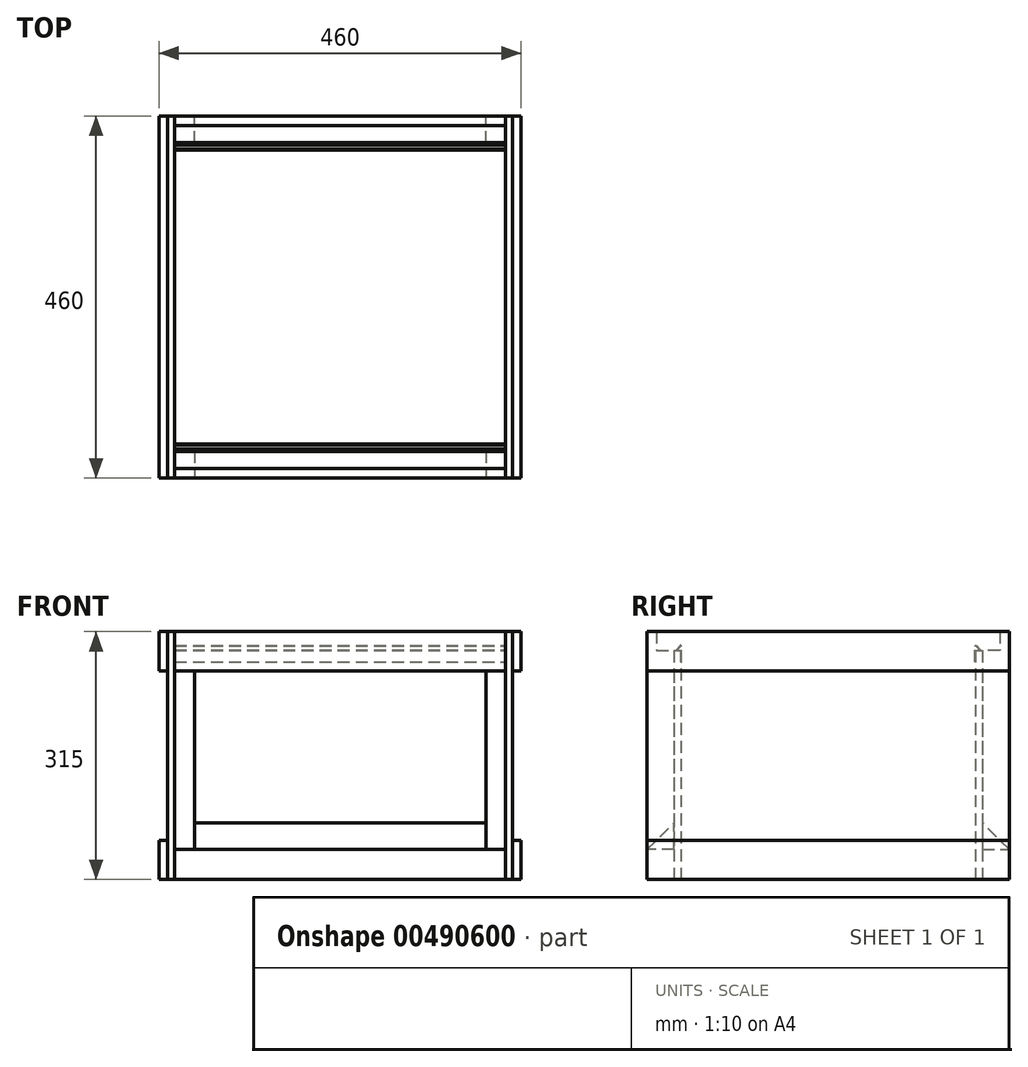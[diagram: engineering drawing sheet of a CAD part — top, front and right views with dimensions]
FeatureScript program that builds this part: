
annotation { "Feature Type Name" : "Feature", "Feature Type Description" : "" }
export const myFeature = defineFeature(function(context is Context, id is Id, definition is map)
    precondition{}
    {
        {
            var Q0;
            Q0=qCreatedBy(makeId("Right.planeOp"),FACE);
            var sketch = newSketch(context, id + "F0", { "sketchPlane" : qUnion([Q0])});
            skLineSegment(sketch, "E0", {"start": v(231.18, 0) * mm, "end": v(231.18, 279.77) * mm, "construction": true});
            skLineSegment(sketch, "E1.right", {"start": v(44.18, 288.91) * mm, "end": v(44.18, -2.09) * mm});
            skLineSegment(sketch, "E2.MirrorCS", {"start": v(418.18, 288.91) * mm, "end": v(418.18, -2.09) * mm});
            skLineSegment(sketch, "E3", {"start": v(35.18, 288.91) * mm, "end": v(35.18, -2.09) * mm});
            skLineSegment(sketch, "E4", {"start": v(427.18, 288.91) * mm, "end": v(427.18, -2.09) * mm});
            skPoint(sketch, "E5.orphan", {"position": v(26.18, 290.5) * mm});
            skPoint(sketch, "E6.MirrorCS.start.orphan", {"position": v(436.18, 290.5) * mm});
            skPoint(sketch, "E1.bottom.end.orphan", {"position": v(44.18, 290.5) * mm});
            skPoint(sketch, "E1.bottom.start.orphan", {"position": v(35.18, 290.5) * mm});
            skPoint(sketch, "E7.MirrorCS.end.orphan", {"position": v(418.18, 290.5) * mm});
            skPoint(sketch, "E7.MirrorCS.start.orphan", {"position": v(427.18, 290.5) * mm});
            skLineSegment(sketch, "E8", {"start": v(35.18, 288.91) * mm, "end": v(44.18, 288.91) * mm});
            skLineSegment(sketch, "E9.trimOffspring", {"start": v(418.18, 288.91) * mm, "end": v(427.18, 288.91) * mm});
            skLineSegment(sketch, "E10.0", {"start": v(35.18, -2.09) * mm, "end": v(44.18, -2.09) * mm});
            skLineSegment(sketch, "E11.0", {"start": v(427.18, -2.09) * mm, "end": v(418.18, -2.09) * mm});
            skPoint(sketch, "E12.MirrorCS.start.orphan", {"position": v(421.18, 288.91) * mm});
            skPoint(sketch, "E13.MirrorCS.end.orphan", {"position": v(418.18, 270.91) * mm});
            skPoint(sketch, "E13.MirrorCS.start.orphan", {"position": v(421.18, 270.91) * mm});
            skPoint(sketch, "E14.start.orphan", {"position": v(41.18, 288.91) * mm});
            skPoint(sketch, "E15.end.orphan", {"position": v(44.18, 270.91) * mm});
            skPoint(sketch, "E15.start.orphan", {"position": v(41.18, 270.91) * mm});
            skSolve(sketch);
        }
        {
            var Q0;
            Q0=qSketchRegion(id+"F0",true);
            extrude(context, id + "F1", {"entities" : qUnion([Q0]), "depth" : 420 * mm, "symmetric" : true});
        }
        {
            var Q0;
            Q0=qCreatedBy(makeId("Right.planeOp"),FACE);
            var sketch = newSketch(context, id + "F2", { "sketchPlane" : qUnion([Q0])});
            skLineSegment(sketch, "E16", {"start": v(1.18, -2.09) * mm, "end": v(1.18, 35.91) * mm});
            skLineSegment(sketch, "E17", {"start": v(231.18, 0) * mm, "end": v(231.18, 279.77) * mm, "construction": true});
            skLineSegment(sketch, "E18", {"start": v(1.18, 312.91) * mm, "end": v(13.18, 312.91) * mm});
            skLineSegment(sketch, "E19", {"start": v(13.18, 312.91) * mm, "end": v(13.18, 288.91) * mm});
            skLineSegment(sketch, "E20", {"start": v(35.18, 262.91) * mm, "end": v(1.18, 262.91) * mm});
            skLineSegment(sketch, "E21", {"start": v(1.18, -2.09) * mm, "end": v(35.18, -2.09) * mm});
            skLineSegment(sketch, "E22", {"start": v(35.18, 35.91) * mm, "end": v(1.18, 35.91) * mm});
            skLineSegment(sketch, "E23.trimOffspring", {"start": v(1.18, 262.91) * mm, "end": v(1.18, 312.91) * mm});
            skLineSegment(sketch, "E24.0", {"start": v(13.18, 288.91) * mm, "end": v(35.18, 288.91) * mm});
            skPoint(sketch, "E25.orphan", {"position": v(35.18, 288.91) * mm});
            skLineSegment(sketch, "E26.0", {"start": v(35.18, 288.91) * mm, "end": v(35.18, 262.91) * mm});
            skPoint(sketch, "E27.orphan", {"position": v(39.86, 35.91) * mm});
            skLineSegment(sketch, "E28.trimOffspring", {"start": v(35.18, 35.91) * mm, "end": v(35.18, -2.09) * mm});
            skPoint(sketch, "E29.orphan", {"position": v(35.18, -2.09) * mm});
            skLineSegment(sketch, "E30.MirrorCS", {"start": v(461.18, 312.91) * mm, "end": v(449.18, 312.91) * mm});
            skLineSegment(sketch, "E31.MirrorCS", {"start": v(449.18, 288.91) * mm, "end": v(427.18, 288.91) * mm});
            skLineSegment(sketch, "E32.MirrorCS", {"start": v(427.18, 288.91) * mm, "end": v(427.18, 262.91) * mm});
            skLineSegment(sketch, "E33.MirrorCS", {"start": v(461.18, -2.09) * mm, "end": v(461.18, 35.91) * mm});
            skPoint(sketch, "E34.MirrorP", {"position": v(427.18, 288.91) * mm});
            skLineSegment(sketch, "E35.MirrorCS", {"start": v(427.18, 262.91) * mm, "end": v(461.18, 262.91) * mm});
            skPoint(sketch, "E36.MirrorP", {"position": v(422.5, 35.91) * mm});
            skLineSegment(sketch, "E37.MirrorCS", {"start": v(461.18, 262.91) * mm, "end": v(461.18, 312.91) * mm});
            skLineSegment(sketch, "E38.MirrorCS", {"start": v(449.18, 312.91) * mm, "end": v(449.18, 288.91) * mm});
            skPoint(sketch, "E39.MirrorP", {"position": v(427.18, -2.09) * mm});
            skLineSegment(sketch, "E40.MirrorCS", {"start": v(427.18, 35.91) * mm, "end": v(461.18, 35.91) * mm});
            skLineSegment(sketch, "E41.MirrorCS", {"start": v(427.18, 35.91) * mm, "end": v(427.18, -2.09) * mm});
            skLineSegment(sketch, "E42.MirrorCS", {"start": v(461.18, -2.09) * mm, "end": v(427.18, -2.09) * mm});
            skSolve(sketch);
        }
        {
            var Q0;
            Q0=qSketchRegion(id+"F2",true);
            extrude(context, id + "F3", {"entities" : qUnion([Q0]), "depth" : 420 * mm, "symmetric" : true});
        }
        {
            var Q0;
            Q0=makeQuery(id+"F1.opExtrude","CAP_FACE",FACE,{"disambiguationData":[OSD([sQuery(id+"F0.wireOp",EDGE,"E1.right"),sQuery(id+"F0.wireOp",EDGE,"E3"),sQuery(id+"F0.wireOp",EDGE,"QR00Nk12-EYIH-hDG3-dkOs-eiUDFboGELUt"),sQuery(id+"F0.wireOp",EDGE,"E8"),sQuery(id+"F0.wireOp",EDGE,"E14"),sQuery(id+"F0.wireOp",EDGE,"E15")])],"isStart":false});
            var sketch = newSketch(context, id + "F4", { "sketchPlane" : qUnion([Q0])});
            skLineSegment(sketch, "E43.1", {"start": v(44.18, 293.91) * mm, "end": v(44.18, 274.51) * mm});
            skLineSegment(sketch, "E44", {"start": v(38.68, 288.91) * mm, "end": v(43.12, 294.3) * mm});
            skArc(sketch, "E45.filletArc", {"start": v(44.18, 293.91) * mm, "mid": v(43.78, 294.48) * mm, "end": v(43.12, 294.3) * mm});
            skLineSegment(sketch, "E46.0", {"start": v(44.73, 293.91) * mm, "end": v(44.73, 274.51) * mm});
            skArc(sketch, "E46.1", {"start": v(44.73, 293.91) * mm, "mid": v(44.52, 294.57) * mm, "end": v(43.97, 295) * mm});
            skLineSegment(sketch, "E46.2", {"start": v(38.25, 289.26) * mm, "end": v(42.7, 294.64) * mm});
            skLineSegment(sketch, "E47", {"start": v(44.73, 274.51) * mm, "end": v(44.18, 274.51) * mm});
            skLineSegment(sketch, "E48", {"start": v(38.25, 289.26) * mm, "end": v(38.68, 288.91) * mm});
            skLineSegment(sketch, "E49", {"start": v(43.2, 295) * mm, "end": v(43.97, 295) * mm});
            skPoint(sketch, "E49.startSnap0", {"position": v(43.97, 295) * mm});
            skArc(sketch, "E50.trimOffspring", {"start": v(43.2, 295) * mm, "mid": v(42.92, 294.85) * mm, "end": v(42.7, 294.64) * mm});
            skPoint(sketch, "E51.orphan", {"position": v(42.8, 295) * mm});
            skSolve(sketch);
        }
        {
            var Q0;
            Q0 = qSketchRegion(id + "F4", true);
            var Q1;
            Q1=makeQuery(id+"F1.opExtrude","CAP_FACE",FACE,{"disambiguationData":[OSD([sQuery(id+"F0.wireOp",EDGE,"E1.right"),sQuery(id+"F0.wireOp",EDGE,"E3"),sQuery(id+"F0.wireOp",EDGE,"QR00Nk12-EYIH-hDG3-dkOs-eiUDFboGELUt"),sQuery(id+"F0.wireOp",EDGE,"E8"),sQuery(id+"F0.wireOp",EDGE,"E14"),sQuery(id+"F0.wireOp",EDGE,"E15")])],"isStart":true});
            extrude(context, id + "F5", {"entities" : qUnion([Q0]), "endBound" : BoundingType.UP_TO_SURFACE, "oppositeDirection" : true, "endBoundEntityFace" : qUnion([Q1]), "depth" : 25.4 * mm});
        }
        {
            var Q0;
            Q0=makeQuery(id+"F1.opExtrude","SWEPT_FACE",FACE,{"disambiguationData":[OSD([sQuery(id+"F0.wireOp",EDGE,"E1.right")])]});
            var Q1;
            Q1=makeQuery(id+"F1.opExtrude","SWEPT_FACE",FACE,{"disambiguationData":[OSD([sQuery(id+"F0.wireOp",EDGE,"E2.MirrorCS")])]});
            cPlane(context, id + "F6", {"entities" : qUnion([Q0, Q1]), "cplaneType" : CPlaneType.MID_PLANE, "offset" : 25 * mm, "width" : 150 * mm, "height" : 150 * mm});
        }
        {
            var Q0;
            Q0=makeQuery(id+"F5.opExtrude","SWEPT_BODY",BODY,{"disambiguationData":[OSD([sQuery(id+"F4.wireOp",EDGE,"E43.0"),sQuery(id+"F4.wireOp",EDGE,"E43.1"),sQuery(id+"F4.wireOp",EDGE,"MzcCW8Xb-HWrt-dKgc-oWSB-JilUSNNGKYap"),sQuery(id+"F4.wireOp",EDGE,"xj4PO2ex-qFnr-YOGi-nNs4-O9hgXSkweLPj"),sQuery(id+"F4.wireOp",EDGE,"05b512f1-f8a8-4a4e-b7e3-4c1ca3ab26b9.filletArc"),sQuery(id+"F4.wireOp",EDGE,"dc7f74d3-6e9f-4502-a8cd-f16476121004.filletArc")])]});
            var Q1;
            Q1=qCreatedBy(id+"F6.planeOp",FACE);
            mirror(context, id + "F7", {"entities" : qUnion([Q0]), "mirrorPlane" : qUnion([Q1])});
        }
        {
            var Q0;
            Q0=makeQuery(id+"F3.opExtrude","CAP_FACE",FACE,{"disambiguationData":[OSD([sQuery(id+"F2.wireOp",EDGE,"E18"),sQuery(id+"F2.wireOp",EDGE,"E19"),sQuery(id+"F2.wireOp",EDGE,"E20"),sQuery(id+"F2.wireOp",EDGE,"E23.trimOffspring"),sQuery(id+"F2.wireOp",EDGE,"82fd9273-c707-4ff1-94b9-1b56f909c31e.0"),sQuery(id+"F2.wireOp",EDGE,"ba24a14a-bd92-40fe-843e-f5e0caba9491.0"),sQuery(id+"F2.wireOp",EDGE,"US8iAf4N-KQBx-rcmz-rff0-gODSU24NLPX8"),sQuery(id+"F2.wireOp",EDGE,"IBiT1izF-VUWa-IY42-BiTY-wa7s07OdXrZS")])],"isStart":false});
            var sketch = newSketch(context, id + "F8", { "sketchPlane" : qUnion([Q0])});
            skLineSegment(sketch, "E52.0", {"start": v(1.18, -2.09) * mm, "end": v(461.18, -2.09) * mm});
            skLineSegment(sketch, "E53.0", {"start": v(1.18, 312.91) * mm, "end": v(13.18, 312.91) * mm});
            skLineSegment(sketch, "E54", {"start": v(1.18, 312.91) * mm, "end": v(1.18, -2.09) * mm});
            skLineSegment(sketch, "E55", {"start": v(13.18, 312.91) * mm, "end": v(461.18, 312.91) * mm});
            skLineSegment(sketch, "E56.0", {"start": v(461.18, -2.09) * mm, "end": v(461.18, 312.91) * mm});
            skSolve(sketch);
        }
        {
            var Q0;
            Q0 = qSketchRegion(id + "F8", true);
            extrude(context, id + "F9", {"entities" : qUnion([Q0]), "depth" : 9 * mm});
        }
        {
            var Q0;
            Q0=makeQuery(id+"F9.opExtrude","SWEPT_FACE",FACE,{"disambiguationData":[OSD([sQuery(id+"F8.wireOp",EDGE,"E54")])]});
            var sketch = newSketch(context, id + "F10", { "sketchPlane" : qUnion([Q0])});
            skLineSegment(sketch, "E57", {"start": v(230, 262.91) * mm, "end": v(230, 312.91) * mm});
            skLineSegment(sketch, "E58.0", {"start": v(230, 312.91) * mm, "end": v(219, 312.91) * mm});
            skPoint(sketch, "E59.orphan", {"position": v(-210, 312.91) * mm});
            skLineSegment(sketch, "E60", {"start": v(219, 155.41) * mm, "end": v(259.35, 155.41) * mm, "construction": true});
            skLineSegment(sketch, "E61", {"start": v(230, 262.91) * mm, "end": v(219, 262.91) * mm});
            skLineSegment(sketch, "E62.0", {"start": v(219, 312.91) * mm, "end": v(219, 262.91) * mm});
            skPoint(sketch, "E63.orphan", {"position": v(219, -2.09) * mm});
            skLineSegment(sketch, "E64.MirrorCS", {"start": v(230, -2.09) * mm, "end": v(219, -2.09) * mm});
            skLineSegment(sketch, "E65.MirrorCS", {"start": v(230, 47.91) * mm, "end": v(219, 47.91) * mm});
            skLineSegment(sketch, "E66.MirrorCS", {"start": v(230, 47.91) * mm, "end": v(230, -2.09) * mm});
            skLineSegment(sketch, "E67.MirrorCS", {"start": v(219, -2.09) * mm, "end": v(219, 47.91) * mm});
            skSolve(sketch);
        }
        {
            var Q0;
            Q0 = qSketchRegion(id + "F10", true);
            var Q1;
            Q1=makeQuery(id+"F9.opExtrude","SWEPT_FACE",FACE,{"disambiguationData":[OSD([sQuery(id+"F8.wireOp",EDGE,"E56.0")])]});
            var Q2;
            Q2=makeQuery(id+"F9.opExtrude","SWEPT_FACE",FACE,{"disambiguationData":[OSD([sQuery(id+"F8.wireOp",EDGE,"fd9dc453-e4fe-45ab-abac-2d0b98b48e28.1")])]});
            extrude(context, id + "F11", {"entities" : qUnion([Q0]), "endBound" : BoundingType.UP_TO_SURFACE, "oppositeDirection" : true, "endBoundEntityFace" : qUnion([Q1]), "depth" : 456.18 * mm});
        }
        {
            var Q0;
            Q0=makeQuery(id+"F9.opExtrude","CAP_FACE",FACE,{"disambiguationData":[OSD([sQuery(id+"F8.wireOp",EDGE,"E52.0"),sQuery(id+"F8.wireOp",EDGE,"E53.0"),sQuery(id+"F8.wireOp",EDGE,"E54"),sQuery(id+"F8.wireOp",EDGE,"E55"),sQuery(id+"F8.wireOp",EDGE,"E56.0")])],"isStart":true});
            var sketch = newSketch(context, id + "F12", { "sketchPlane" : qUnion([Q0])});
            skLineSegment(sketch, "E68.1", {"start": v(-35.18, 263.52) * mm, "end": v(-35.18, 35.91) * mm});
            skLineSegment(sketch, "E69.2", {"start": v(-35.18, 262.91) * mm, "end": v(-1.18, 262.91) * mm});
            skLineSegment(sketch, "E69.3", {"start": v(-35.18, 35.91) * mm, "end": v(-1.18, 35.91) * mm});
            skLineSegment(sketch, "E70.0", {"start": v(-1.18, 262.91) * mm, "end": v(-1.18, 35.91) * mm});
            skPoint(sketch, "E71.orphan", {"position": v(-35.18, 288.91) * mm});
            skPoint(sketch, "E72.orphan", {"position": v(-1.18, 262.91) * mm});
            skPoint(sketch, "E73.orphan", {"position": v(-35.18, -2.09) * mm});
            skPoint(sketch, "E74.orphan", {"position": v(-1.18, 35.91) * mm});
            skLineSegment(sketch, "E75", {"start": v(-231.18, -2.09) * mm, "end": v(-231.18, 143.1) * mm, "construction": true});
            skPoint(sketch, "E76.MirrorP", {"position": v(-461.18, 35.91) * mm});
            skLineSegment(sketch, "E77.MirrorCS", {"start": v(-427.18, 35.91) * mm, "end": v(-461.18, 35.91) * mm});
            skLineSegment(sketch, "E78.MirrorCS", {"start": v(-427.18, 262.91) * mm, "end": v(-461.18, 262.91) * mm});
            skPoint(sketch, "E79.MirrorP", {"position": v(-461.18, 262.91) * mm});
            skLineSegment(sketch, "E80.MirrorCS", {"start": v(-427.18, 263.52) * mm, "end": v(-427.18, 35.91) * mm});
            skLineSegment(sketch, "E81.MirrorCS", {"start": v(-461.18, 262.91) * mm, "end": v(-461.18, 35.91) * mm});
            skPoint(sketch, "E82.MirrorP", {"position": v(-427.18, 288.91) * mm});
            skPoint(sketch, "E83.MirrorP", {"position": v(-427.18, -2.09) * mm});
            skSolve(sketch);
        }
        {
            var Q0;
            Q0 = qSketchRegion(id + "F12", true);
            extrude(context, id + "F13", {"entities" : qUnion([Q0]), "offsetDistance" : 25 * mm, "depth" : 25 * mm});
        }
        {
            var Q0;
            Q0=makeQuery(id+"F9.opExtrude","SWEPT_BODY",BODY,{"disambiguationData":[OSD([sQuery(id+"F8.wireOp",EDGE,"E52.0"),sQuery(id+"F8.wireOp",EDGE,"E53.0"),sQuery(id+"F8.wireOp",EDGE,"E54"),sQuery(id+"F8.wireOp",EDGE,"E55"),sQuery(id+"F8.wireOp",EDGE,"E56.0")])]});
            var Q1;
            Q1=makeQuery(id+"F11.opExtrude","SWEPT_BODY",BODY,{"disambiguationData":[OSD([sQuery(id+"F10.wireOp",EDGE,"E64.MirrorCS"),sQuery(id+"F10.wireOp",EDGE,"E65.MirrorCS"),sQuery(id+"F10.wireOp",EDGE,"E66.MirrorCS"),sQuery(id+"F10.wireOp",EDGE,"E67.MirrorCS")])]});
            var Q2;
            Q2=makeQuery(id+"F11.opExtrude","SWEPT_BODY",BODY,{"disambiguationData":[OSD([sQuery(id+"F10.wireOp",EDGE,"E57"),sQuery(id+"F10.wireOp",EDGE,"E58.0"),sQuery(id+"F10.wireOp",EDGE,"E61"),sQuery(id+"F10.wireOp",EDGE,"E62.0")])]});
            var Q3;
            Q3=makeQuery(id+"F13.opExtrude","SWEPT_BODY",BODY,{"disambiguationData":[OSD([sQuery(id+"F12.wireOp",EDGE,"E68.1"),sQuery(id+"F12.wireOp",EDGE,"E69.2"),sQuery(id+"F12.wireOp",EDGE,"E69.3"),sQuery(id+"F12.wireOp",EDGE,"E70.0")])]});
            var Q4;
            Q4=makeQuery(id+"F13.opExtrude","SWEPT_BODY",BODY,{"disambiguationData":[OSD([sQuery(id+"F12.wireOp",EDGE,"E77.MirrorCS"),sQuery(id+"F12.wireOp",EDGE,"E78.MirrorCS"),sQuery(id+"F12.wireOp",EDGE,"E80.MirrorCS"),sQuery(id+"F12.wireOp",EDGE,"E81.MirrorCS")])]});
            var Q5;
            Q5=qCreatedBy(makeId("Right.planeOp"),FACE);
            mirror(context, id + "F14", {"entities" : qUnion([Q0, Q1, Q2, Q3, Q4]), "mirrorPlane" : qUnion([Q5])});
        }
        {
            var Q0;
            Q0=makeQuery(id+"F13.opExtrude","CAP_FACE",FACE,{"disambiguationData":[OSD([sQuery(id+"F12.wireOp",EDGE,"E68.1"),sQuery(id+"F12.wireOp",EDGE,"E69.2"),sQuery(id+"F12.wireOp",EDGE,"E69.3"),sQuery(id+"F12.wireOp",EDGE,"E70.0")])],"isStart":false});
            var sketch = newSketch(context, id + "F15", { "sketchPlane" : qUnion([Q0])});
            skLineSegment(sketch, "E84.0", {"start": v(-35.18, 35.91) * mm, "end": v(-1.18, 35.91) * mm});
            skLineSegment(sketch, "E85", {"start": v(-35.18, 35.91) * mm, "end": v(-35.18, 69.91) * mm});
            skLineSegment(sketch, "E86", {"start": v(-35.18, 69.91) * mm, "end": v(-1.18, 35.91) * mm});
            skLineSegment(sketch, "E87.MirrorCS", {"start": v(-427.18, 69.91) * mm, "end": v(-461.18, 35.91) * mm});
            skLineSegment(sketch, "E88.MirrorCS", {"start": v(-427.18, 35.91) * mm, "end": v(-461.18, 35.91) * mm});
            skLineSegment(sketch, "E89.MirrorCS", {"start": v(-427.18, 35.91) * mm, "end": v(-427.18, 69.91) * mm});
            skSolve(sketch);
        }
        {
            var Q0;
            Q0 = qSketchRegion(id + "F15", true);
            var Q1;
            Q1=makeQuery(id+"F14.opPattern","COPY",FACE,{"derivedFrom":makeQuery(id+"F13.opExtrude","CAP_FACE",FACE,{"disambiguationData":[OSD([sQuery(id+"F12.wireOp",EDGE,"E68.1"),sQuery(id+"F12.wireOp",EDGE,"E69.2"),sQuery(id+"F12.wireOp",EDGE,"E69.3"),sQuery(id+"F12.wireOp",EDGE,"E70.0")])],"isStart":false}),"instanceName":"1"});
            extrude(context, id + "F16", {"entities" : qUnion([Q0]), "endBound" : BoundingType.UP_TO_SURFACE, "depth" : 25 * mm, "endBoundEntityFace" : qUnion([Q1]), "offsetDistance" : 25 * mm});
        }
    });
